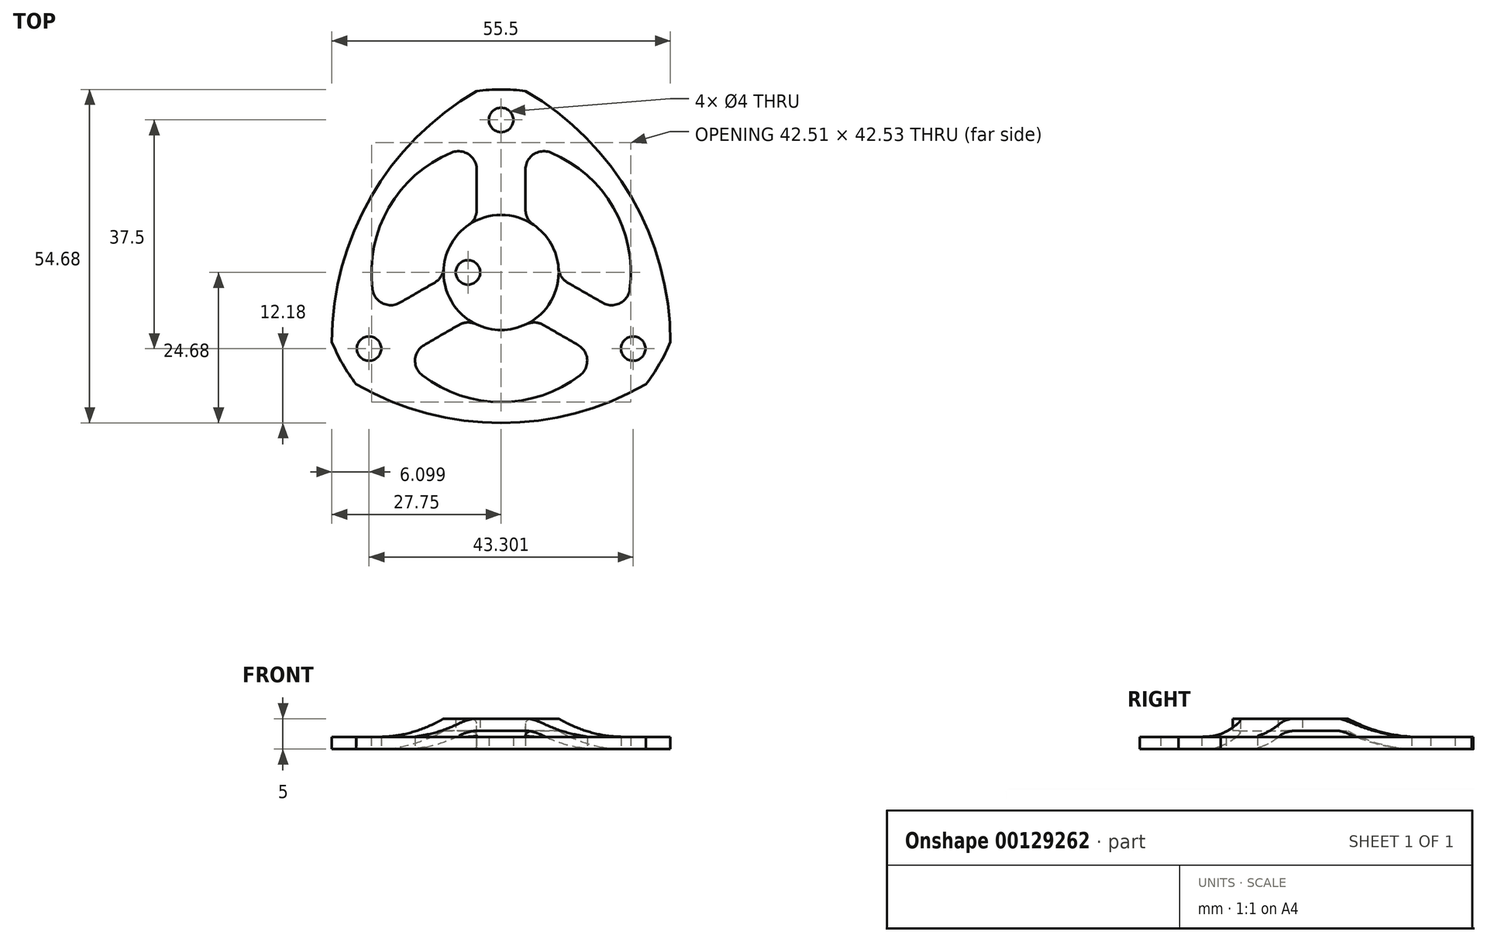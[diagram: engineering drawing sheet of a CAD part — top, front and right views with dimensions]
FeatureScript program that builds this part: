
annotation { "Feature Type Name" : "Feature", "Feature Type Description" : "" }
export const myFeature = defineFeature(function(context is Context, id is Id, definition is map)
    precondition{}
    {
        {
            var Q0;
            Q0=qCreatedBy(makeId("Top.planeOp"),FACE);
            var sketch = newSketch(context, id + "F0", { "sketchPlane" : qUnion([Q0])});
            skLineSegment(sketch, "E0", {"start": v(0, 17.53) * mm, "end": v(0, -19.48) * mm, "construction": true});
            skLineSegment(sketch, "E1", {"start": v(-21.26, 0) * mm, "end": v(21.59, 0) * mm, "construction": true});
            skCircle(sketch, "E2", {"center": v(-5.43, 0) * mm, "radius": 2 * mm});
            skCircle(sketch, "E3.MirrorC", {"center": v(5.43, 0) * mm, "radius": 2 * mm});
            skLineSegment(sketch, "E4.0", {"start": v(-21.26, 25) * mm, "end": v(21.59, 25) * mm, "construction": true});
            skLineSegment(sketch, "E5", {"start": v(0, 17.53) * mm, "end": v(0, 28.93) * mm, "construction": true});
            skCircle(sketch, "E6", {"center": v(0, 25) * mm, "radius": 2 * mm});
            skCircle(sketch, "E7.1.0", {"center": v(-21.65, -12.5) * mm, "radius": 2 * mm});
            skCircle(sketch, "E7.2.0", {"center": v(21.65, -12.5) * mm, "radius": 2 * mm});
            skPoint(sketch, "E7.center", {"position": v(0, 0) * mm});
            skSolve(sketch);
        }
        {
            var Q0;
            Q0=qCreatedBy(makeId("Front.planeOp"),FACE);
            var sketch = newSketch(context, id + "F1", { "sketchPlane" : qUnion([Q0])});
            skLineSegment(sketch, "E8.0", {"start": v(-7.43, 0) * mm, "end": v(21.59, 0) * mm, "construction": true});
            skLineSegment(sketch, "E9.0", {"start": v(-7.43, 0) * mm, "end": v(-3.43, 0) * mm, "construction": true});
            skLineSegment(sketch, "E10", {"start": v(0, 12.59) * mm, "end": v(0, -3.02) * mm, "construction": true});
            skLineSegment(sketch, "E11.0", {"start": v(-30, 5) * mm, "end": v(-30, -3.02) * mm, "construction": true});
            skLineSegment(sketch, "E12.0", {"start": v(-7.43, 2) * mm, "end": v(21.59, 2) * mm, "construction": true});
            skLineSegment(sketch, "E13.0", {"start": v(-9.43, 5) * mm, "end": v(21.59, 5) * mm, "construction": true});
            skLineSegment(sketch, "E14.0", {"start": v(-9.43, 3) * mm, "end": v(21.59, 3) * mm, "construction": true});
            skLineSegment(sketch, "E15", {"start": v(-21.26, 5) * mm, "end": v(-32.77, 5) * mm, "construction": true});
            skLineSegment(sketch, "E16", {"start": v(-21.26, 0) * mm, "end": v(-30, 0) * mm});
            skLineSegment(sketch, "E17", {"start": v(-30, 0) * mm, "end": v(-30, 2) * mm});
            skLineSegment(sketch, "E18", {"start": v(-30, 2) * mm, "end": v(-21.26, 2) * mm});
            skLineSegment(sketch, "E19", {"start": v(-7.43, 0) * mm, "end": v(-7.43, 2) * mm, "construction": true});
            skLineSegment(sketch, "E20.trimOffspring", {"start": v(-7.43, 3) * mm, "end": v(-7.43, 5) * mm, "construction": true});
            skLineSegment(sketch, "E21.0", {"start": v(-9.43, 3) * mm, "end": v(-9.43, 5) * mm, "construction": true});
            skLineSegment(sketch, "E22", {"start": v(-9.43, 5) * mm, "end": v(0, 5) * mm});
            skLineSegment(sketch, "E23", {"start": v(0, 5) * mm, "end": v(0, 3) * mm});
            skLineSegment(sketch, "E24", {"start": v(0, 3) * mm, "end": v(-9.43, 3) * mm});
            skArc(sketch, "E25", {"start": v(-21.26, 2) * mm, "mid": v(-15.16, 2.76) * mm, "end": v(-9.43, 5) * mm});
            skArc(sketch, "E26", {"start": v(-21.26, 0) * mm, "mid": v(-15.16, 0.76) * mm, "end": v(-9.43, 3) * mm});
            skSolve(sketch);
        }
        {
            var Q0;
            Q0=makeQuery(id+"F1.imprint","IMPRINT",FACE,{"disambiguationData":[TD([[makeQuery(id+"F1.imprint","IMPRINT",EDGE,{"derivedFrom":sQuery(id+"F1.wireOp",EDGE,"E16")}),-1.0]])]});
            var Q1;
            Q1=sQuery(id+"F1.wireOp",EDGE,"E23");
            revolve(context, id + "F2", {"entities" : qUnion([Q0]), "axis" : qUnion([Q1]), "revolveType" : RevolveType.FULL});
        }
        {
            var Q0;
            Q0=makeQuery(id+"F0.imprint","IMPRINT",FACE,{"disambiguationData":[TD([[makeQuery(id+"F0.imprint","IMPRINT",EDGE,{"derivedFrom":sQuery(id+"F0.wireOp",EDGE,"E6")}),1.0]])]});
            var Q1;
            Q1=makeQuery(id+"F0.imprint","IMPRINT",FACE,{"disambiguationData":[TD([[makeQuery(id+"F0.imprint","IMPRINT",EDGE,{"derivedFrom":sQuery(id+"F0.wireOp",EDGE,"E3.MirrorC")}),-1.0]])]});
            var Q2;
            Q2=makeQuery(id+"F0.imprint","IMPRINT",FACE,{"disambiguationData":[TD([[makeQuery(id+"F0.imprint","IMPRINT",EDGE,{"derivedFrom":sQuery(id+"F0.wireOp",EDGE,"E2")}),1.0]])]});
            var Q3;
            Q3=makeQuery(id+"F0.imprint","IMPRINT",FACE,{"disambiguationData":[TD([[makeQuery(id+"F0.imprint","IMPRINT",EDGE,{"derivedFrom":sQuery(id+"F0.wireOp",EDGE,"E7.2.0")}),1.0]])]});
            var Q4;
            Q4=makeQuery(id+"F0.imprint","IMPRINT",FACE,{"disambiguationData":[TD([[makeQuery(id+"F0.imprint","IMPRINT",EDGE,{"derivedFrom":sQuery(id+"F0.wireOp",EDGE,"E7.1.0")}),1.0]])]});
            extrude(context, id + "F3", {"entities" : qUnion([Q0, Q1, Q2, Q3, Q4]), "operationType" : NewBodyOperationType.REMOVE, "depth" : 25 * mm});
        }
        {
            var Q0;
            Q0=qCreatedBy(makeId("Top.planeOp"),FACE);
            var sketch = newSketch(context, id + "F4", { "sketchPlane" : qUnion([Q0])});
            skCircle(sketch, "E27.0", {"center": v(0, 0) * mm, "radius": 21.26 * mm});
            skCircle(sketch, "E28.0", {"center": v(0, 0) * mm, "radius": 30 * mm});
            skCircle(sketch, "E29.0", {"center": v(0, 0) * mm, "radius": 9.43 * mm});
            skLineSegment(sketch, "E30", {"start": v(0, 0) * mm, "end": v(0, 36.5) * mm, "construction": true});
            skLineSegment(sketch, "E31.0", {"start": v(4, 0) * mm, "end": v(4, 36.5) * mm, "construction": true});
            skLineSegment(sketch, "E32.0", {"start": v(-4, 0) * mm, "end": v(-4, 36.5) * mm, "construction": true});
            skLineSegment(sketch, "E33", {"start": v(-4, 20.89) * mm, "end": v(-4, 8.54) * mm});
            skLineSegment(sketch, "E34", {"start": v(4, 8.54) * mm, "end": v(4, 20.89) * mm});
            skLineSegment(sketch, "E35.1.0", {"start": v(-2, 3.46) * mm, "end": v(-33.6, -14.78) * mm, "construction": true});
            skLineSegment(sketch, "E35.1.1", {"start": v(2, -3.46) * mm, "end": v(-29.6, -21.7) * mm, "construction": true});
            skLineSegment(sketch, "E35.2.0", {"start": v(-2, -3.46) * mm, "end": v(29.6, -21.7) * mm, "construction": true});
            skLineSegment(sketch, "E35.2.1", {"start": v(2, 3.46) * mm, "end": v(33.6, -14.78) * mm, "construction": true});
            skLineSegment(sketch, "E36", {"start": v(-16.09, -13.9) * mm, "end": v(-5.4, -7.74) * mm});
            skLineSegment(sketch, "E37", {"start": v(-9.4, -0.8) * mm, "end": v(-20.09, -6.98) * mm});
            skLineSegment(sketch, "E38", {"start": v(5.4, -7.74) * mm, "end": v(16.09, -13.9) * mm});
            skLineSegment(sketch, "E39", {"start": v(9.4, -0.8) * mm, "end": v(20.09, -6.98) * mm});
            skArc(sketch, "E40", {"start": v(27.75, -11.4) * mm, "mid": v(21.37, 12.34) * mm, "end": v(4, 29.73) * mm});
            skArc(sketch, "E41.1.0", {"start": v(-4, 29.73) * mm, "mid": v(-21.37, 12.34) * mm, "end": v(-27.75, -11.4) * mm});
            skArc(sketch, "E41.2.0", {"start": v(-23.75, -18.33) * mm, "mid": v(0, -24.68) * mm, "end": v(23.75, -18.33) * mm});
            skSolve(sketch);
        }
        {
            var Q0;
            {var subQ0=sQuery(id+"F4.wireOp",EDGE,"E41.1.0");Q0=makeQuery(id+"F4.imprint","IMPRINT",FACE,{"disambiguationData":[TD([[makeQuery(id+"F4.imprint","IMPRINT",EDGE,{"derivedFrom":subQ0}),-1.0]])]});}
            var Q1;
            {var subQ0=sQuery(id+"F4.wireOp",EDGE,"E41.2.0");Q1=makeQuery(id+"F4.imprint","IMPRINT",FACE,{"disambiguationData":[TD([[makeQuery(id+"F4.imprint","IMPRINT",EDGE,{"derivedFrom":subQ0}),-1.0]])]});}
            var Q2;
            {var subQ0=sQuery(id+"F4.wireOp",EDGE,"E36");Q2=makeQuery(id+"F4.imprint","IMPRINT",FACE,{"disambiguationData":[TD([[makeQuery(id+"F4.imprint","IMPRINT",EDGE,{"derivedFrom":subQ0}),-1.0]])]});}
            var Q3;
            {var subQ0=sQuery(id+"F4.wireOp",EDGE,"E34");Q3=makeQuery(id+"F4.imprint","IMPRINT",FACE,{"disambiguationData":[TD([[makeQuery(id+"F4.imprint","IMPRINT",EDGE,{"derivedFrom":subQ0}),-1.0]])]});}
            var Q4;
            {var subQ0=sQuery(id+"F4.wireOp",EDGE,"E40");Q4=makeQuery(id+"F4.imprint","IMPRINT",FACE,{"disambiguationData":[TD([[makeQuery(id+"F4.imprint","IMPRINT",EDGE,{"derivedFrom":subQ0}),-1.0]])]});}
            var Q5;
            {var subQ0=sQuery(id+"F4.wireOp",EDGE,"E33");Q5=makeQuery(id+"F4.imprint","IMPRINT",FACE,{"disambiguationData":[TD([[makeQuery(id+"F4.imprint","IMPRINT",EDGE,{"derivedFrom":subQ0}),-1.0]])]});}
            extrude(context, id + "F5", {"entities" : qUnion([Q0, Q1, Q2, Q3, Q4, Q5]), "operationType" : NewBodyOperationType.REMOVE, "depth" : 25 * mm});
        }
        {
            var Q0;
            Q0=makeQuery(id+"F5.boolean.opBoolean","COPY",EDGE,{"derivedFrom":makeQuery(id+"F5.opExtrude","SWEPT_EDGE",EDGE,{"disambiguationData":[OSD([sQuery(id+"F4.wireOp",EDGE,"E29.0"),sQuery(id+"F4.wireOp",EDGE,"E39")])]})});
            var Q1;
            Q1=makeQuery(id+"F5.boolean.opBoolean","COPY",EDGE,{"derivedFrom":makeQuery(id+"F5.opExtrude","SWEPT_EDGE",EDGE,{"disambiguationData":[OSD([sQuery(id+"F4.wireOp",EDGE,"E27.0"),sQuery(id+"F4.wireOp",EDGE,"E39")])]})});
            var Q2;
            Q2=makeQuery(id+"F5.boolean.opBoolean","COPY",EDGE,{"derivedFrom":makeQuery(id+"F5.opExtrude","SWEPT_EDGE",EDGE,{"disambiguationData":[OSD([sQuery(id+"F4.wireOp",EDGE,"E29.0"),sQuery(id+"F4.wireOp",EDGE,"E34")])]})});
            var Q3;
            Q3=makeQuery(id+"F5.boolean.opBoolean","COPY",EDGE,{"derivedFrom":makeQuery(id+"F5.opExtrude","SWEPT_EDGE",EDGE,{"disambiguationData":[OSD([sQuery(id+"F4.wireOp",EDGE,"E27.0"),sQuery(id+"F4.wireOp",EDGE,"E34")])]})});
            var Q4;
            Q4=makeQuery(id+"F5.boolean.opBoolean","COPY",EDGE,{"derivedFrom":makeQuery(id+"F5.opExtrude","SWEPT_EDGE",EDGE,{"disambiguationData":[OSD([sQuery(id+"F4.wireOp",EDGE,"E29.0"),sQuery(id+"F4.wireOp",EDGE,"E33")])]})});
            var Q5;
            Q5=makeQuery(id+"F5.boolean.opBoolean","COPY",EDGE,{"derivedFrom":makeQuery(id+"F5.opExtrude","SWEPT_EDGE",EDGE,{"disambiguationData":[OSD([sQuery(id+"F4.wireOp",EDGE,"E27.0"),sQuery(id+"F4.wireOp",EDGE,"E33")])]})});
            var Q6;
            Q6=makeQuery(id+"F5.boolean.opBoolean","COPY",EDGE,{"derivedFrom":makeQuery(id+"F5.opExtrude","SWEPT_EDGE",EDGE,{"disambiguationData":[OSD([sQuery(id+"F4.wireOp",EDGE,"E29.0"),sQuery(id+"F4.wireOp",EDGE,"E37")])]})});
            var Q7;
            Q7=makeQuery(id+"F5.boolean.opBoolean","COPY",EDGE,{"derivedFrom":makeQuery(id+"F5.opExtrude","SWEPT_EDGE",EDGE,{"disambiguationData":[OSD([sQuery(id+"F4.wireOp",EDGE,"E27.0"),sQuery(id+"F4.wireOp",EDGE,"E37")])]})});
            var Q8;
            Q8=makeQuery(id+"F5.boolean.opBoolean","COPY",EDGE,{"derivedFrom":makeQuery(id+"F5.opExtrude","SWEPT_EDGE",EDGE,{"disambiguationData":[OSD([sQuery(id+"F4.wireOp",EDGE,"E29.0"),sQuery(id+"F4.wireOp",EDGE,"E38")])]})});
            var Q9;
            Q9=makeQuery(id+"F5.boolean.opBoolean","COPY",EDGE,{"derivedFrom":makeQuery(id+"F5.opExtrude","SWEPT_EDGE",EDGE,{"disambiguationData":[OSD([sQuery(id+"F4.wireOp",EDGE,"E29.0"),sQuery(id+"F4.wireOp",EDGE,"E36")])]})});
            var Q10;
            Q10=makeQuery(id+"F5.boolean.opBoolean","COPY",EDGE,{"derivedFrom":makeQuery(id+"F5.opExtrude","SWEPT_EDGE",EDGE,{"disambiguationData":[OSD([sQuery(id+"F4.wireOp",EDGE,"E27.0"),sQuery(id+"F4.wireOp",EDGE,"E36")])]})});
            var Q11;
            Q11=makeQuery(id+"F5.boolean.opBoolean","COPY",EDGE,{"derivedFrom":makeQuery(id+"F5.opExtrude","SWEPT_EDGE",EDGE,{"disambiguationData":[OSD([sQuery(id+"F4.wireOp",EDGE,"E27.0"),sQuery(id+"F4.wireOp",EDGE,"E38")])]})});
            fillet(context, id + "F6", {"entities" : qUnion([Q0, Q1, Q2, Q3, Q4, Q5, Q6, Q7, Q8, Q9, Q10, Q11]), "radius" : 3 * mm, "tangentPropagation" : true, "allowEdgeOverflow" : false});
        }
    });
